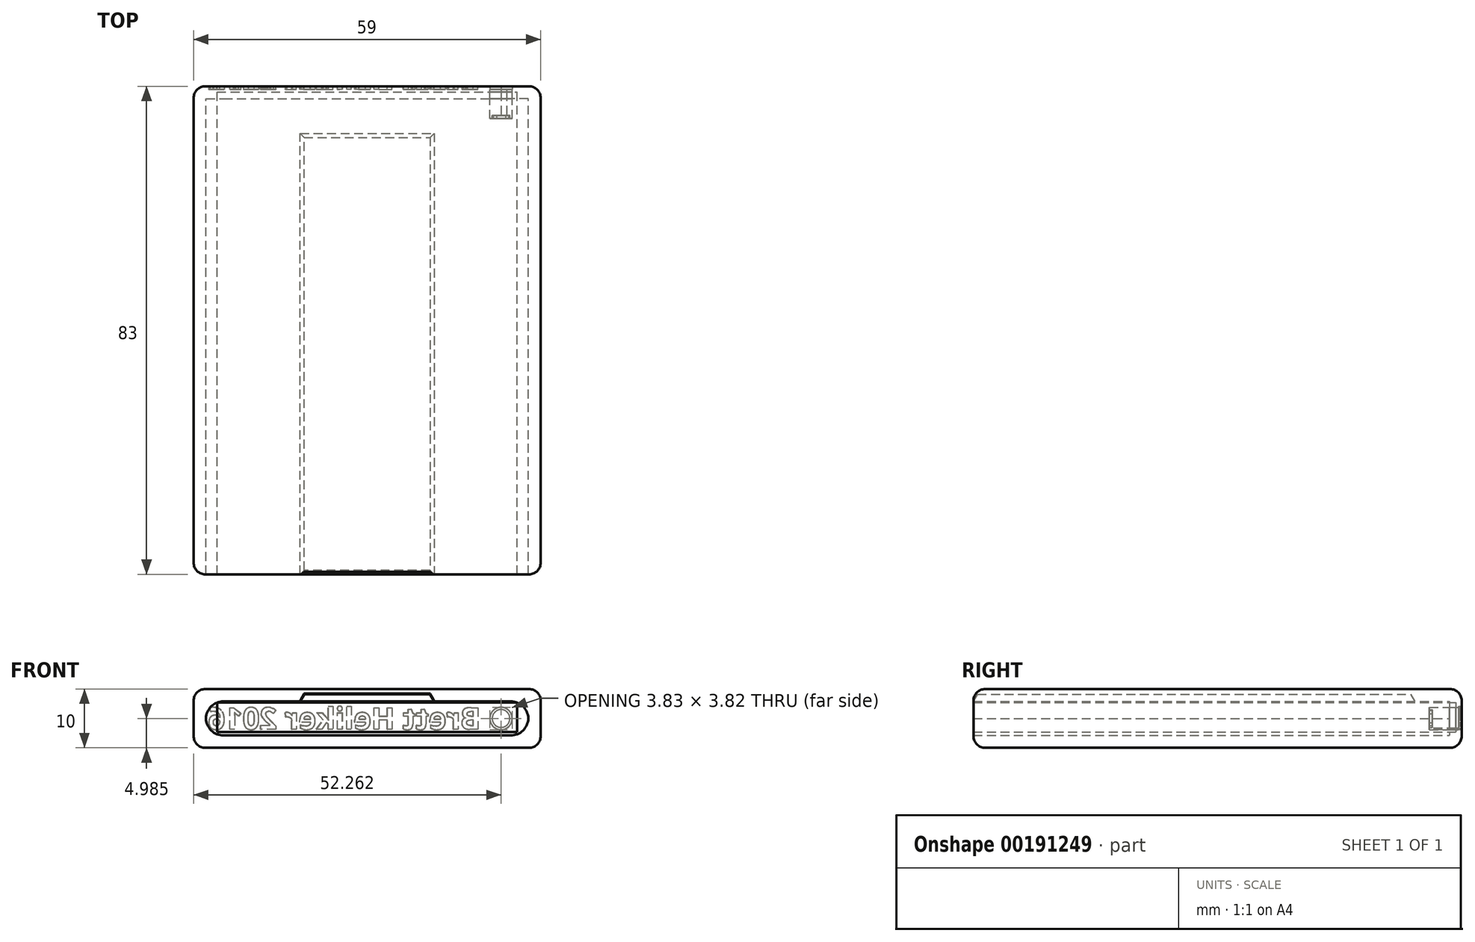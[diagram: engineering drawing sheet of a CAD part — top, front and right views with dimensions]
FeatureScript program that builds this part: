
annotation { "Feature Type Name" : "Feature", "Feature Type Description" : "" }
export const myFeature = defineFeature(function(context is Context, id is Id, definition is map)
    precondition{}
    {
        {
            var Q0;
            Q0=qCreatedBy(makeId("Top.planeOp"),FACE);
            var sketch = newSketch(context, id + "F0", { "sketchPlane" : qUnion([Q0])});
            skLineSegment(sketch, "E0.bottom", {"start": v(0, 0) * mm, "end": v(51, 0) * mm});
            skLineSegment(sketch, "E0.top", {"start": v(0, 82) * mm, "end": v(51, 82) * mm});
            skLineSegment(sketch, "E0.left", {"start": v(0, 0) * mm, "end": v(0, 82) * mm});
            skLineSegment(sketch, "E0.right", {"start": v(51, 0) * mm, "end": v(51, 82) * mm});
            skSolve(sketch);
        }
        {
            var Q0;
            Q0=makeQuery(id+"F0.imprint","IMPRINT",FACE,{"disambiguationData":[TD([[makeQuery(id+"F0.imprint","IMPRINT",EDGE,{"derivedFrom":sQuery(id+"F0.wireOp",EDGE,"E0.bottom")}),1.0]])]});
            extrude(context, id + "F1", {"entities" : qUnion([Q0]), "depth" : 5 * mm});
        }
        {
            var Q0;
            Q0=qCreatedBy(makeId("Top.planeOp"),FACE);
            var sketch = newSketch(context, id + "F2", { "sketchPlane" : qUnion([Q0])});
            skLineSegment(sketch, "E1.bottom", {"start": v(-4, 0) * mm, "end": v(55, 0) * mm});
            skLineSegment(sketch, "E1.top", {"start": v(-4, 83) * mm, "end": v(55, 83) * mm});
            skLineSegment(sketch, "E1.left", {"start": v(-4, 0) * mm, "end": v(-4, 83) * mm});
            skLineSegment(sketch, "E1.right", {"start": v(55, 0) * mm, "end": v(55, 83) * mm});
            skSolve(sketch);
        }
        {
            var Q0;
            Q0 = qSketchRegion(id + "F2", true);
            extrude(context, id + "F3", {"entities" : qUnion([Q0]), "depth" : 10 * mm});
        }
        {
            var Q0;
            Q0=makeQuery(id+"F3.opExtrude","SWEPT_FACE",FACE,{"disambiguationData":[OSD([sQuery(id+"F2.wireOp",EDGE,"E1.bottom")])]});
            shell(context, id + "F4", {"entities" : qUnion([Q0]), "thickness" : 2.1 * mm});
        }
        {
            var Q0;
            {var subQ0=sQuery(id+"F2.wireOp",EDGE,"E1.left");Q0=makeQuery(id+"F4.opShell","OFFSET_EDGE",EDGE,{"disambiguationData":[OSD([subQ0]),TDD([makeQuery(id+"F3.opExtrude","CAP_EDGE",EDGE,{"disambiguationData":[OSD([subQ0])],"isStart":false})])]});}
            var Q1;
            {var subQ0=sQuery(id+"F2.wireOp",EDGE,"E1.right");Q1=makeQuery(id+"F4.opShell","OFFSET_EDGE",EDGE,{"disambiguationData":[OSD([subQ0]),TDD([makeQuery(id+"F3.opExtrude","CAP_EDGE",EDGE,{"disambiguationData":[OSD([subQ0])],"isStart":true})])]});}
            var Q2;
            {var subQ0=sQuery(id+"F2.wireOp",EDGE,"E1.right");Q2=makeQuery(id+"F4.opShell","OFFSET_EDGE",EDGE,{"disambiguationData":[OSD([subQ0]),TDD([makeQuery(id+"F3.opExtrude","CAP_EDGE",EDGE,{"disambiguationData":[OSD([subQ0])],"isStart":false})])]});}
            var Q3;
            {var subQ0=sQuery(id+"F2.wireOp",EDGE,"E1.left");Q3=makeQuery(id+"F4.opShell","OFFSET_EDGE",EDGE,{"disambiguationData":[OSD([subQ0]),TDD([makeQuery(id+"F3.opExtrude","CAP_EDGE",EDGE,{"disambiguationData":[OSD([subQ0])],"isStart":true})])]});}
            fillet(context, id + "F5", {"entities" : qUnion([Q0, Q1, Q2, Q3]), "radius" : 3 * mm, "tangentPropagation" : true, "allowEdgeOverflow" : false});
        }
        {
            var Q0;
            Q0=makeQuery(id+"F3.opExtrude","CAP_EDGE",EDGE,{"disambiguationData":[OSD([sQuery(id+"F2.wireOp",EDGE,"E1.left")])],"isStart":false});
            var Q1;
            Q1=makeQuery(id+"F3.opExtrude","CAP_EDGE",EDGE,{"disambiguationData":[OSD([sQuery(id+"F2.wireOp",EDGE,"E1.left")])],"isStart":true});
            var Q2;
            Q2=makeQuery(id+"F3.opExtrude","CAP_EDGE",EDGE,{"disambiguationData":[OSD([sQuery(id+"F2.wireOp",EDGE,"E1.right")])],"isStart":false});
            var Q3;
            Q3=makeQuery(id+"F3.opExtrude","CAP_EDGE",EDGE,{"disambiguationData":[OSD([sQuery(id+"F2.wireOp",EDGE,"E1.right")])],"isStart":true});
            var Q4;
            Q4=makeQuery(id+"F3.opExtrude","SWEPT_EDGE",EDGE,{"disambiguationData":[OSD([sQuery(id+"F2.wireOp",EDGE,"E1.top"),sQuery(id+"F2.wireOp",EDGE,"E1.right")])]});
            var Q5;
            Q5=makeQuery(id+"F3.opExtrude","CAP_EDGE",EDGE,{"disambiguationData":[OSD([sQuery(id+"F2.wireOp",EDGE,"E1.top")])],"isStart":false});
            var Q6;
            Q6=makeQuery(id+"F3.opExtrude","CAP_EDGE",EDGE,{"disambiguationData":[OSD([sQuery(id+"F2.wireOp",EDGE,"E1.top")])],"isStart":true});
            var Q7;
            Q7=makeQuery(id+"F3.opExtrude","SWEPT_EDGE",EDGE,{"disambiguationData":[OSD([sQuery(id+"F2.wireOp",EDGE,"E1.top"),sQuery(id+"F2.wireOp",EDGE,"E1.left")])]});
            var Q8;
            Q8=makeQuery(id+"F3.opExtrude","CAP_EDGE",EDGE,{"disambiguationData":[OSD([sQuery(id+"F2.wireOp",EDGE,"E1.bottom")])],"isStart":false});
            var Q9;
            Q9=makeQuery(id+"F3.opExtrude","SWEPT_EDGE",EDGE,{"disambiguationData":[OSD([sQuery(id+"F2.wireOp",EDGE,"E1.bottom"),sQuery(id+"F2.wireOp",EDGE,"E1.right")])]});
            var Q10;
            Q10=makeQuery(id+"F3.opExtrude","CAP_EDGE",EDGE,{"disambiguationData":[OSD([sQuery(id+"F2.wireOp",EDGE,"E1.bottom")])],"isStart":true});
            var Q11;
            Q11=makeQuery(id+"F3.opExtrude","SWEPT_EDGE",EDGE,{"disambiguationData":[OSD([sQuery(id+"F2.wireOp",EDGE,"E1.bottom"),sQuery(id+"F2.wireOp",EDGE,"E1.left")])]});
            fillet(context, id + "F6", {"entities" : qUnion([Q0, Q1, Q2, Q3, Q4, Q5, Q6, Q7, Q8, Q9, Q10, Q11]), "radius" : 2 * mm, "tangentPropagation" : true, "allowEdgeOverflow" : false});
        }
        {
            var Q0;
            {var subQ0=sQuery(id+"F2.wireOp",EDGE,"E1.right");var subQ1=sQuery(id+"F2.wireOp",EDGE,"E1.left");var subQ2=sQuery(id+"F2.wireOp",EDGE,"E1.top");var subQ3=sQuery(id+"F2.wireOp",EDGE,"E1.bottom");Q0=makeQuery(id+"F4.opShell","OFFSET_FACE",FACE,{"disambiguationData":[OSD([subQ3,subQ2,subQ1,subQ0]),TDD([makeQuery(id+"F3.opExtrude","CAP_FACE",FACE,{"disambiguationData":[OSD([subQ3,subQ2,subQ1,subQ0])],"isStart":false})])]});}
            var sketch = newSketch(context, id + "F7", { "sketchPlane" : qUnion([Q0])});
            skLineSegment(sketch, "E2.bottom", {"start": v(14.1, 0) * mm, "end": v(36.9, 0) * mm});
            skLineSegment(sketch, "E2.top", {"start": v(14.1, -75) * mm, "end": v(36.9, -75) * mm});
            skLineSegment(sketch, "E2.left", {"start": v(14.1, 0) * mm, "end": v(14.1, -75) * mm});
            skLineSegment(sketch, "E2.right", {"start": v(36.9, 0) * mm, "end": v(36.9, -75) * mm});
            skSolve(sketch);
        }
        {
            var Q0;
            Q0=makeQuery(id+"F7.imprint","IMPRINT",FACE,{"disambiguationData":[TD([[makeQuery(id+"F7.imprint","IMPRINT",EDGE,{"derivedFrom":sQuery(id+"F7.wireOp",EDGE,"E2.bottom")}),-1.0]])]});
            extrude(context, id + "F8", {"entities" : qUnion([Q0]), "operationType" : NewBodyOperationType.REMOVE, "oppositeDirection" : true, "depth" : 1.2 * mm, "hasDraft" : true, "draftAngle" : 30 * degree, "draftPullDirection" : true});
        }
        {
            var Q0;
            Q0=makeQuery(id+"F3.opExtrude","SWEPT_FACE",FACE,{"disambiguationData":[OSD([sQuery(id+"F2.wireOp",EDGE,"E1.top")])]});
            var sketch = newSketch(context, id + "F9", { "sketchPlane" : qUnion([Q0])});
            skText(sketch, "E3", { "text": "<copyright redacted>
            const initialGuessF9  = {"E3": [-0.0504, 0.00315, 1, 0, 0.0037]};
            skSetInitialGuess(sketch, initialGuessF9);
            skSolve(sketch);
        }
        {
            var Q0;
            Q0 = qSketchRegion(id + "F9", true);
            extrude(context, id + "F10", {"entities" : qUnion([Q0]), "operationType" : NewBodyOperationType.REMOVE, "oppositeDirection" : true, "depth" : 0.5 * mm, "hasDraft" : true, "draftAngle" : 3 * degree});
        }
        {
            var Q0;
            Q0=makeQuery(id+"F1.opExtrude","SWEPT_BODY",BODY,{"disambiguationData":[OSD([sQuery(id+"F0.wireOp",EDGE,"E0.bottom"),sQuery(id+"F0.wireOp",EDGE,"E0.top"),sQuery(id+"F0.wireOp",EDGE,"E0.left"),sQuery(id+"F0.wireOp",EDGE,"E0.right")])]});
            transform(context, id + "F11", {"entities" : qUnion([Q0]), "transformType" : TransformType.TRANSLATION_3D, "dx" : 0 * mm, "dy" : 0 * mm, "dz" : 2.7 * mm, "makeCopy" : false});
        }
        {
            var Q0;
            Q0=makeQuery(id+"F8.boolean.opBoolean","COPY",FACE,{"derivedFrom":makeQuery(id+"F8.opExtrude","SWEPT_FACE",FACE,{"disambiguationData":[OSD([sQuery(id+"F7.wireOp",EDGE,"E2.bottom")])]})});
            extrude(context, id + "F12", {"entities" : qUnion([Q0]), "operationType" : NewBodyOperationType.REMOVE, "oppositeDirection" : true, "depth" : 25 * mm});
        }
        {
            var Q0;
            Q0=makeQuery(id+"F10.boolean.opBoolean","SPLIT",FACE,{"disambiguationData":[TD([makeQuery(id+"F10.opExtrude","SWEPT_FACE",FACE,{"disambiguationData":[OSD([sQuery(id+"F9.wireOp",EDGE,"E3.sketch_text.stroke-26")])]})])],"derivedFrom":makeQuery(id+"F3.opExtrude","SWEPT_FACE",FACE,{"disambiguationData":[OSD([sQuery(id+"F2.wireOp",EDGE,"E1.top")])]})});
            var Q1;
            Q1=makeQuery(id+"F10.boolean.opBoolean","COPY",FACE,{"derivedFrom":makeQuery(id+"F10.opExtrude","CAP_FACE",FACE,{"disambiguationData":[OSD([sQuery(id+"F9.wireOp",EDGE,"E3.sketch_text.stroke-14"),sQuery(id+"F9.wireOp",EDGE,"E3.sketch_text.stroke-15"),sQuery(id+"F9.wireOp",EDGE,"E3.sketch_text.stroke-16"),sQuery(id+"F9.wireOp",EDGE,"E3.sketch_text.stroke-17"),sQuery(id+"F9.wireOp",EDGE,"E3.sketch_text.stroke-18"),sQuery(id+"F9.wireOp",EDGE,"E3.sketch_text.stroke-19"),sQuery(id+"F9.wireOp",EDGE,"E3.sketch_text.stroke-20"),sQuery(id+"F9.wireOp",EDGE,"E3.sketch_text.stroke-21"),sQuery(id+"F9.wireOp",EDGE,"E3.sketch_text.stroke-22"),sQuery(id+"F9.wireOp",EDGE,"E3.sketch_text.stroke-23"),sQuery(id+"F9.wireOp",EDGE,"E3.sketch_text.stroke-24"),sQuery(id+"F9.wireOp",EDGE,"E3.sketch_text.stroke-25"),sQuery(id+"F9.wireOp",EDGE,"E3.sketch_text.stroke-26"),sQuery(id+"F9.wireOp",EDGE,"E3.sketch_text.stroke-27"),sQuery(id+"F9.wireOp",EDGE,"E3.sketch_text.stroke-28"),sQuery(id+"F9.wireOp",EDGE,"E3.sketch_text.stroke-29"),sQuery(id+"F9.wireOp",EDGE,"E3.sketch_text.stroke-30"),sQuery(id+"F9.wireOp",EDGE,"E3.sketch_text.stroke-31"),sQuery(id+"F9.wireOp",EDGE,"E3.sketch_text.stroke-32"),sQuery(id+"F9.wireOp",EDGE,"E3.sketch_text.stroke-33"),sQuery(id+"F9.wireOp",EDGE,"E3.sketch_text.stroke-34"),sQuery(id+"F9.wireOp",EDGE,"E3.sketch_text.stroke-35"),sQuery(id+"F9.wireOp",EDGE,"E3.sketch_text.stroke-36"),sQuery(id+"F9.wireOp",EDGE,"E3.sketch_text.stroke-37")])],"isStart":false})});
            extrude(context, id + "F13", {"entities" : qUnion([Q0, Q1]), "operationType" : NewBodyOperationType.REMOVE, "oppositeDirection" : true, "depth" : 5 * mm});
        }
    });
